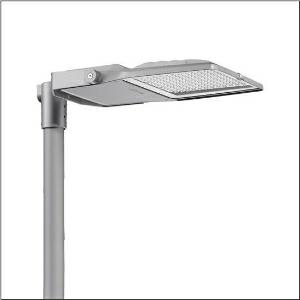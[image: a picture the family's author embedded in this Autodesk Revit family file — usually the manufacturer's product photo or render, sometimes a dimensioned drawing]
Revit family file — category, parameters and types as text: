
# Revit family: floodlight_fl_21_midi___pl52_5xa7785f2d3a_eb33
name_source: partatom
category: Lighting Fixtures
units: mm (PartAtom-declared; Revit-internal decimal feet)

## family parameters
Cut with Voids When Loaded = No
Host = Face
Light Source = No
Part Type = Normal
Room Calculation Point = No
Round Connector Dimension = Use Diameter
Shared = No

## types (1)
- --- (1 x LED, 35750 lm, 271.6 W, 3000K)
    Apparent Load = 272 VA
    CIE Flux Codes = 26 60 98 100 100
    Color Rendering = 70
    Color Temperature = 3000K
    Default Elevation = 1800 mm
    Description = Floodlight FL 21 midi, floodlight, primary light control with lens, of PMMA, primary optical cover: protective disc, of toughened safety glass, transparent, light distribution: PL52, light emission: direct distribution, installation type: surface-mounted, LED, High Power LED, rated luminous flux: 35.750lm, luminous efficacy: 132lm/W, light colour: 730, colour temperature: 3000K, control gear: Smart Interface (Zhaga), control: flexible luminous flux parameterisation, time-dependent luminous flux control, constant luminous flux control, overheat protection, pre-setting: logarithmic dimming characteristic, with terminal, 6-pole, mains connection: 220..240V, AC, 50/60Hz, start of lifetime: 272W, end of service life: 287W, reduction: 123W, luminaire housing, of diecast aluminium, powder-coated, Siteco® metallic grey (DB 702S), corrosivity category C5 mid according to DIN EN ISO 12944, suitable for swimming pools, chlorine-resistant, sealing non-destructively replaceable, please order mast flange separately, mast bracket, of steel, galvanised, powder-coated, Siteco® metallic grey (DB 702S), Smart Interface above, protection rating (complete): IP66, insulation class (complete): insulation class II (safety insulation), certification: CE, ENEC, VDE, protection symbol: D, impact resistance: IK08, permissible operating ambient temperature: -40..+40°C, permissible operating ambient temperature for outdoor applications: -40..+50°C, standard: DIN EN 12944, LABS conformity tested according to VDMA 24364:2018-05, packaging unit: 1 piece

Light Distribution: PL52
    Height = 76 mm
    Lamp = 1 x LED
    Lamp Light Flux = 35750 lm
    Lamp Power = 271.6 W
    Lamp count = 1
    Length = 657 mm
    Luminous efficacy = 132 lm/W
    Manufacturer = Siteco
    ModVariant = No
    Model = 5XA7785F2D3A
    Number of Poles = 1
    OnlyDefault = Yes
    Power Factor = 1
    Product Name = Floodlight FL 21 midi | PL52
    Product group = floodlight | pylon annexe
    ProductGroupID = 6200
    Protection Class = Protection class II
    Protection Degree = IP 66
    RLX_Detail_Level = 1
    RLX_Emergency_Light_Flux = 0 lm
    RLX_Emergency_Type = 0
    RLX_Emergency_Type_DB = No
    RlxData = <blob elided: 154161 chars, md5=e78e06b3>
    Socket = socket
    Standby Power = 0 W
    System Light Flux = 35750 lm
    System Power = 272 W
    Type Comments = factory setting: luminous flux: 100 % | dim-lin: 254 | 620 mA
    Type Image = l_1007123.jpg
    URL = http://relux.com
    VarID = @adj_177478
    Voltage = 0 V
    Weight = 0.00 kg
    Width = 442 mm

## geometry (parser evidence)
native form markers: Blend x4, Sweep x12
no freeform markers — native parametric forms only
